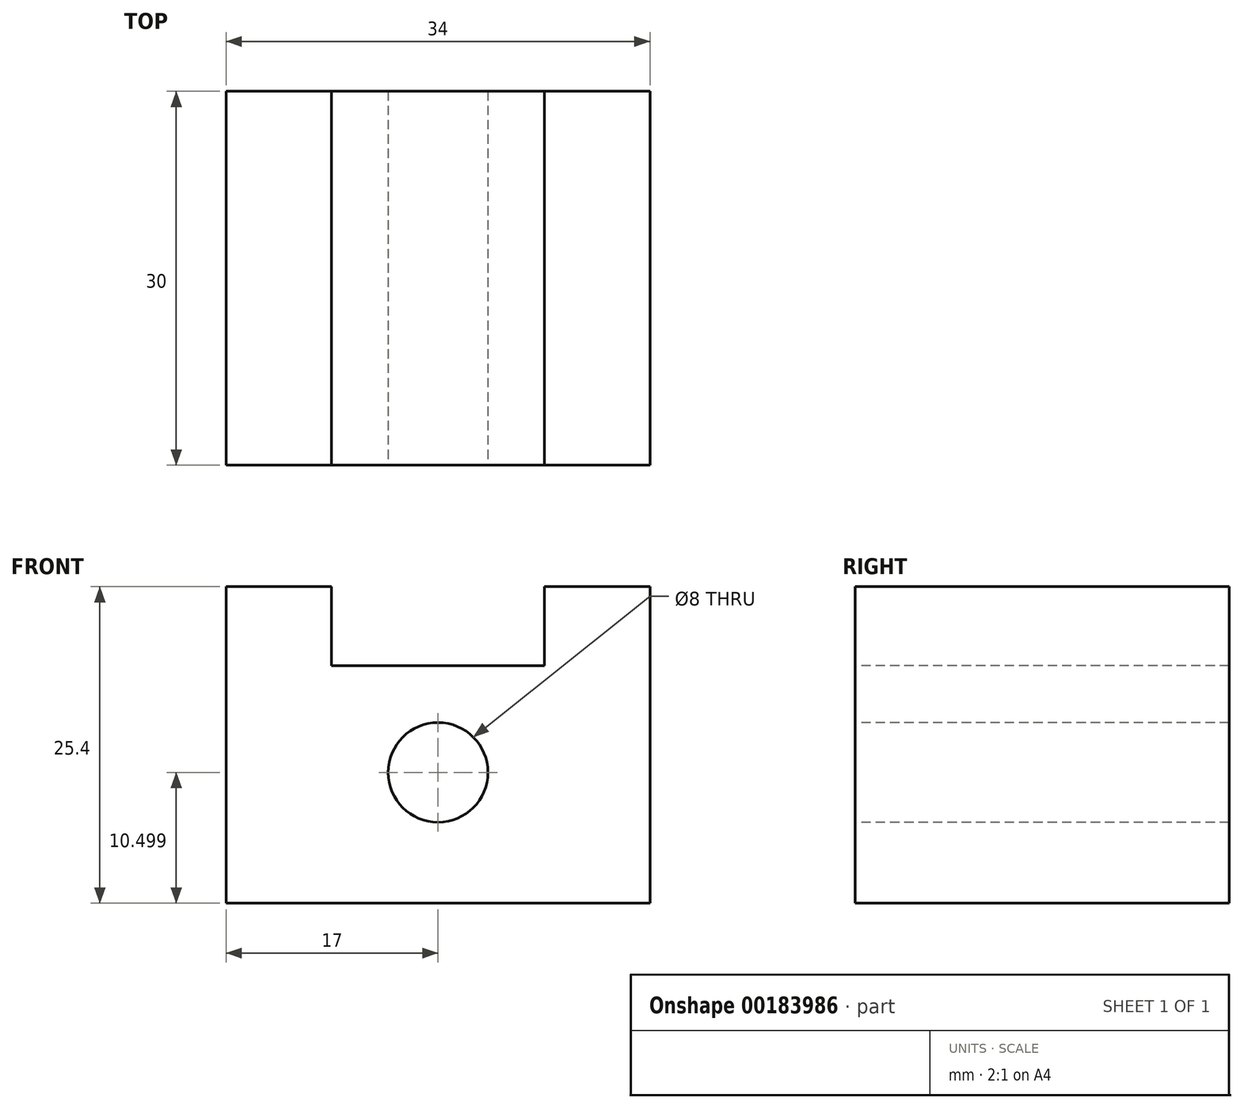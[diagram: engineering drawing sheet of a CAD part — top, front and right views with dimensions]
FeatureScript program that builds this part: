
annotation { "Feature Type Name" : "Feature", "Feature Type Description" : "" }
export const myFeature = defineFeature(function(context is Context, id is Id, definition is map)
    precondition{}
    {
        {
            var Q0;
            Q0=qCreatedBy(makeId("Top.planeOp"),FACE);
            var sketch = newSketch(context, id + "F0", { "sketchPlane" : qUnion([Q0])});
            skLineSegment(sketch, "E0.bottom", {"start": v(17, 15) * mm, "end": v(-17, 15) * mm});
            skLineSegment(sketch, "E0.top", {"start": v(17, -15) * mm, "end": v(-17, -15) * mm});
            skLineSegment(sketch, "E0.left", {"start": v(17, 15) * mm, "end": v(17, -15) * mm});
            skLineSegment(sketch, "E0.right", {"start": v(-17, 15) * mm, "end": v(-17, -15) * mm});
            skPoint(sketch, "E0.middle", {"position": v(0, 0) * mm});
            skSolve(sketch);
        }
        {
            var Q0;
            Q0 = qSketchRegion(id + "F0", true);
            extrude(context, id + "F1", {"entities" : qUnion([Q0]), "depth" : 25.4 * mm});
        }
        {
            var Q0;
            Q0=makeQuery(id+"F1.opExtrude","SWEPT_FACE",FACE,{"disambiguationData":[OSD([sQuery(id+"F0.wireOp",EDGE,"E0.top")])]});
            var sketch = newSketch(context, id + "F2", { "sketchPlane" : qUnion([Q0])});
            skCircle(sketch, "E1", {"center": v(0, 10.5) * mm, "radius": 4 * mm});
            skSolve(sketch);
        }
        {
            var Q0;
            Q0=makeQuery(id+"F2.imprint","IMPRINT",FACE,{"disambiguationData":[TD([[makeQuery(id+"F2.imprint","IMPRINT",EDGE,{"derivedFrom":sQuery(id+"F2.wireOp",EDGE,"E1")}),1.0]])]});
            extrude(context, id + "F3", {"entities" : qUnion([Q0]), "operationType" : NewBodyOperationType.REMOVE, "endBound" : BoundingType.THROUGH_ALL, "oppositeDirection" : true, "depth" : 25.4 * mm});
        }
        {
            var Q0;
            Q0=makeQuery(id+"F1.opExtrude","CAP_FACE",FACE,{"disambiguationData":[OSD([sQuery(id+"F0.wireOp",EDGE,"E0.bottom"),sQuery(id+"F0.wireOp",EDGE,"E0.top"),sQuery(id+"F0.wireOp",EDGE,"E0.left"),sQuery(id+"F0.wireOp",EDGE,"E0.right")])],"isStart":false});
            var sketch = newSketch(context, id + "F4", { "sketchPlane" : qUnion([Q0])});
            skLineSegment(sketch, "E2.bottom", {"start": v(8.54, 15) * mm, "end": v(-8.54, 15) * mm});
            skLineSegment(sketch, "E2.top", {"start": v(8.54, -15) * mm, "end": v(-8.54, -15) * mm});
            skLineSegment(sketch, "E2.left", {"start": v(8.54, 15) * mm, "end": v(8.54, -15) * mm});
            skLineSegment(sketch, "E2.right", {"start": v(-8.54, 15) * mm, "end": v(-8.54, -15) * mm});
            skPoint(sketch, "E2.middle", {"position": v(0, 0) * mm});
            skSolve(sketch);
        }
        {
            var Q0;
            Q0 = qSketchRegion(id + "F4", true);
            extrude(context, id + "F5", {"entities" : qUnion([Q0]), "operationType" : NewBodyOperationType.REMOVE, "oppositeDirection" : true, "depth" : 6.35 * mm});
        }
    });
